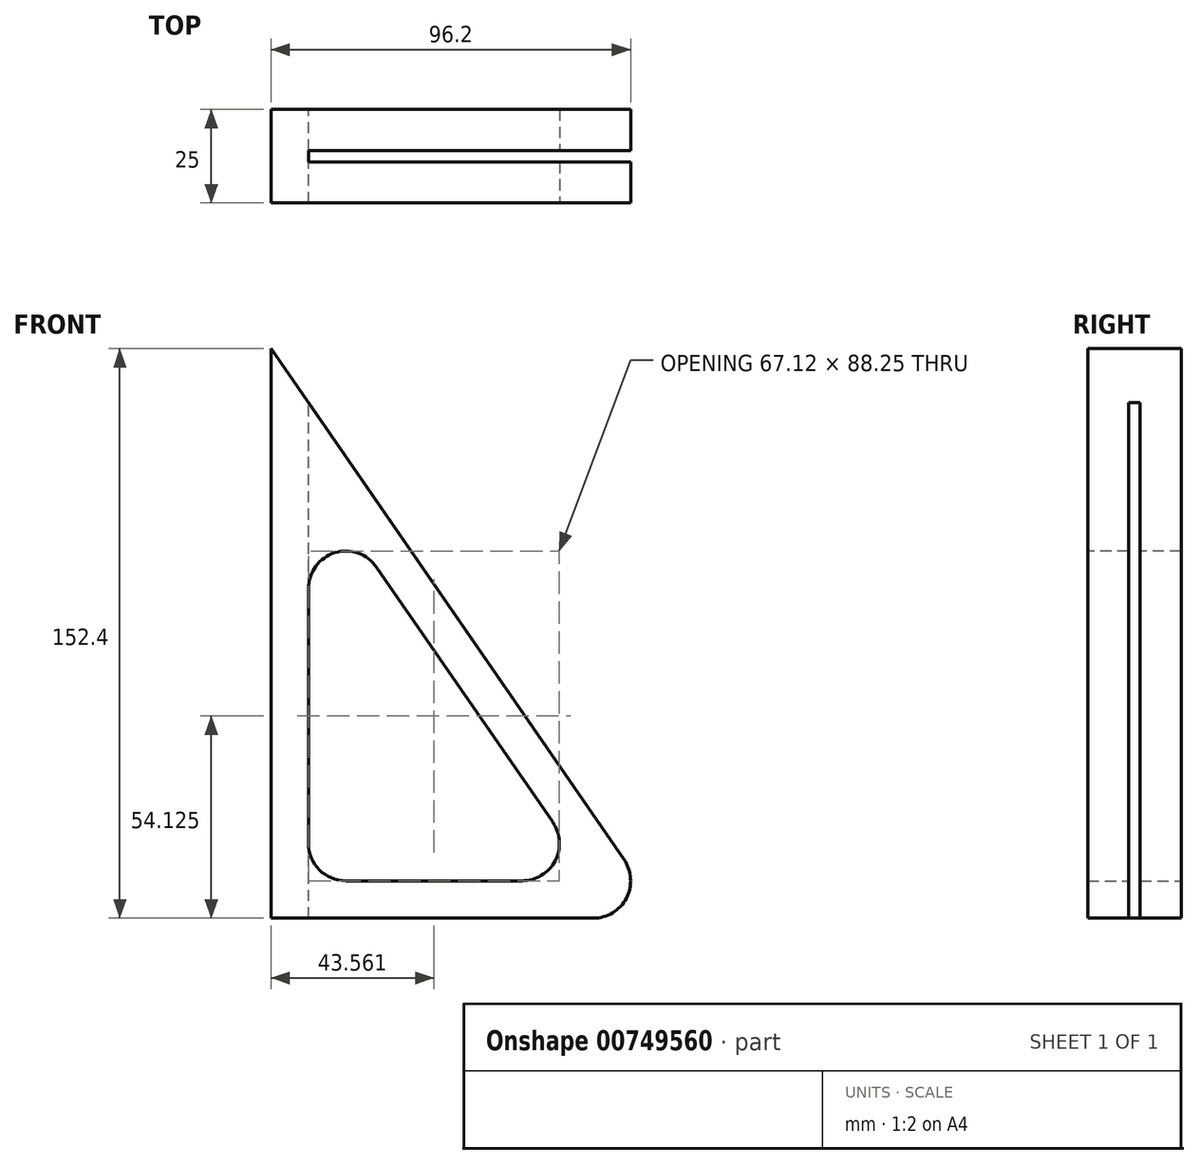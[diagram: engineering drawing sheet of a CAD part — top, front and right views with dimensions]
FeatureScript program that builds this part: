
annotation { "Feature Type Name" : "Feature", "Feature Type Description" : "" }
export const myFeature = defineFeature(function(context is Context, id is Id, definition is map)
    precondition{}
    {
        {
            var Q0;
            Q0=qCreatedBy(makeId("Front.planeOp"),FACE);
            var sketch = newSketch(context, id + "F0", { "sketchPlane" : qUnion([Q0])});
            skLineSegment(sketch, "E0", {"start": v(10, 120.33) * mm, "end": v(10, 10) * mm});
            skLineSegment(sketch, "E1", {"start": v(10, 10) * mm, "end": v(86.2, 10) * mm});
            skLineSegment(sketch, "E2", {"start": v(86.2, 10) * mm, "end": v(10, 120.33) * mm});
            skLineSegment(sketch, "E3", {"start": v(105.26, 10) * mm, "end": v(105.26, 0) * mm});
            skLineSegment(sketch, "E4", {"start": v(105.26, 0) * mm, "end": v(0, 0) * mm});
            skLineSegment(sketch, "E5", {"start": v(0, 0) * mm, "end": v(0, 152.4) * mm});
            skLineSegment(sketch, "E6", {"start": v(0, 152.4) * mm, "end": v(98.35, 10) * mm});
            skLineSegment(sketch, "E7", {"start": v(98.35, 10) * mm, "end": v(105.26, 10) * mm});
            skLineSegment(sketch, "E8", {"start": v(98.35, 10) * mm, "end": v(105.26, 0) * mm});
            skLineSegment(sketch, "E9", {"start": v(86.2, 10) * mm, "end": v(93.1, 0) * mm});
            skSolve(sketch);
        }
        {
            var Q0;
            Q0=makeQuery(id+"F0.imprint","IMPRINT",FACE,{"disambiguationData":[TD([[makeQuery(id+"F0.imprint","IMPRINT",EDGE,{"derivedFrom":sQuery(id+"F0.wireOp",EDGE,"E0")}),-1.0]])]});
            extrude(context, id + "F1", {"entities" : qUnion([Q0]), "depth" : 25 * mm, "offsetDistance" : 25 * mm});
        }
        {
            var Q0;
            Q0=qCreatedBy(makeId("Right.planeOp"),FACE);
            cPlane(context, id + "F2", {"entities" : qUnion([Q0]), "cplaneType" : CPlaneType.OFFSET, "offset" : 163 * mm, "width" : 150 * mm, "height" : 150 * mm});
        }
        {
            var Q0;
            Q0=qCreatedBy(id+"F2.planeOp",FACE);
            var sketch = newSketch(context, id + "F3", { "sketchPlane" : qUnion([Q0])});
            skLineSegment(sketch, "E10.bottom", {"start": v(-10.95, 197.6) * mm, "end": v(-14.05, 197.6) * mm});
            skLineSegment(sketch, "E10.top", {"start": v(-10.95, -197.6) * mm, "end": v(-14.05, -197.6) * mm});
            skLineSegment(sketch, "E10.left", {"start": v(-10.95, 197.6) * mm, "end": v(-10.95, -197.6) * mm});
            skLineSegment(sketch, "E10.right", {"start": v(-14.05, 197.6) * mm, "end": v(-14.05, -197.6) * mm});
            skPoint(sketch, "E10.middle", {"position": v(-12.5, 0) * mm});
            skSolve(sketch);
        }
        {
            var Q0;
            Q0 = qSketchRegion(id + "F3", true);
            var Q1;
            Q1=makeQuery(id+"F1.opExtrude","SWEPT_FACE",FACE,{"disambiguationData":[OSD([sQuery(id+"F0.wireOp",EDGE,"E0")])]});
            extrude(context, id + "F4", {"entities" : qUnion([Q0]), "operationType" : NewBodyOperationType.REMOVE, "endBound" : BoundingType.UP_TO_SURFACE, "oppositeDirection" : true, "depth" : 25 * mm, "endBoundEntityFace" : qUnion([Q1]), "offsetDistance" : 25 * mm});
        }
        {
            var Q0;
            {var subQ0=sQuery(id+"F0.wireOp",EDGE,"E8");var subQ2=sQuery(id+"F0.wireOp",EDGE,"E4");Q0=makeQuery(id+"F4.boolean.opBoolean","SPLIT",EDGE,{"disambiguationData":[TD([makeQuery(id+"F4.opExtrude","SWEPT_FACE",FACE,{"disambiguationData":[OSD([sQuery(id+"F3.wireOp",EDGE,"E10.right")])]})])],"derivedFrom":makeQuery(id+"F1.opExtrude","SWEPT_EDGE",EDGE,{"disambiguationData":[OSD([sQuery(id+"F0.wireOp",EDGE,"E3"),subQ2,subQ0])]})});}
            var Q1;
            {var subQ0=sQuery(id+"F0.wireOp",EDGE,"E8");var subQ2=sQuery(id+"F0.wireOp",EDGE,"E4");Q1=makeQuery(id+"F4.boolean.opBoolean","SPLIT",EDGE,{"disambiguationData":[TD([makeQuery(id+"F4.opExtrude","SWEPT_FACE",FACE,{"disambiguationData":[OSD([sQuery(id+"F3.wireOp",EDGE,"E10.left")])]})])],"derivedFrom":makeQuery(id+"F1.opExtrude","SWEPT_EDGE",EDGE,{"disambiguationData":[OSD([sQuery(id+"F0.wireOp",EDGE,"E3"),subQ2,subQ0])]})});}
            var Q2;
            {var subQ0=sQuery(id+"F3.wireOp",EDGE,"E10.right");var subQ1=sQuery(id+"F0.wireOp",EDGE,"E1");var subQ2=sQuery(id+"F0.wireOp",EDGE,"E0");Q2=makeQuery(id+"F4.boolean.opBoolean","SPLIT",EDGE,{"disambiguationData":[TD([makeQuery(id+"F4.opExtrude","SWEPT_FACE",FACE,{"disambiguationData":[OSD([subQ0])]})])],"derivedFrom":makeQuery(id+"F1.opExtrude","SWEPT_EDGE",EDGE,{"disambiguationData":[OSD([subQ2,subQ1])]})});}
            var Q3;
            {var subQ0=sQuery(id+"F0.wireOp",EDGE,"E1");var subQ1=sQuery(id+"F3.wireOp",EDGE,"E10.left");var subQ2=sQuery(id+"F0.wireOp",EDGE,"E0");Q3=makeQuery(id+"F4.boolean.opBoolean","SPLIT",EDGE,{"disambiguationData":[TD([makeQuery(id+"F4.opExtrude","SWEPT_FACE",FACE,{"disambiguationData":[OSD([subQ1])]})])],"derivedFrom":makeQuery(id+"F1.opExtrude","SWEPT_EDGE",EDGE,{"disambiguationData":[OSD([subQ2,subQ0])]})});}
            var Q4;
            {var subQ0=sQuery(id+"F0.wireOp",EDGE,"E2");var subQ1=sQuery(id+"F3.wireOp",EDGE,"E10.left");var subQ2=sQuery(id+"F0.wireOp",EDGE,"E0");Q4=makeQuery(id+"F4.boolean.opBoolean","SPLIT",EDGE,{"disambiguationData":[TD([makeQuery(id+"F4.opExtrude","SWEPT_FACE",FACE,{"disambiguationData":[OSD([subQ1])]})])],"derivedFrom":makeQuery(id+"F1.opExtrude","SWEPT_EDGE",EDGE,{"disambiguationData":[OSD([subQ2,subQ0])]})});}
            var Q5;
            {var subQ0=sQuery(id+"F3.wireOp",EDGE,"E10.right");var subQ1=sQuery(id+"F0.wireOp",EDGE,"E2");var subQ2=sQuery(id+"F0.wireOp",EDGE,"E0");Q5=makeQuery(id+"F4.boolean.opBoolean","SPLIT",EDGE,{"disambiguationData":[TD([makeQuery(id+"F4.opExtrude","SWEPT_FACE",FACE,{"disambiguationData":[OSD([subQ0])]})])],"derivedFrom":makeQuery(id+"F1.opExtrude","SWEPT_EDGE",EDGE,{"disambiguationData":[OSD([subQ2,subQ1])]})});}
            var Q6;
            {var subQ0=sQuery(id+"F0.wireOp",EDGE,"E2");var subQ1=sQuery(id+"F0.wireOp",EDGE,"E1");Q6=makeQuery(id+"F4.boolean.opBoolean","SPLIT",EDGE,{"disambiguationData":[TD([makeQuery(id+"F4.opExtrude","SWEPT_FACE",FACE,{"disambiguationData":[OSD([sQuery(id+"F3.wireOp",EDGE,"E10.right")])]})])],"derivedFrom":makeQuery(id+"F1.opExtrude","SWEPT_EDGE",EDGE,{"disambiguationData":[OSD([subQ1,subQ0])]})});}
            var Q7;
            {var subQ0=sQuery(id+"F0.wireOp",EDGE,"E2");var subQ1=sQuery(id+"F0.wireOp",EDGE,"E1");Q7=makeQuery(id+"F4.boolean.opBoolean","SPLIT",EDGE,{"disambiguationData":[TD([makeQuery(id+"F4.opExtrude","SWEPT_FACE",FACE,{"disambiguationData":[OSD([sQuery(id+"F3.wireOp",EDGE,"E10.left")])]})])],"derivedFrom":makeQuery(id+"F1.opExtrude","SWEPT_EDGE",EDGE,{"disambiguationData":[OSD([subQ1,subQ0])]})});}
            fillet(context, id + "F5", {"entities" : qUnion([Q0, Q1, Q2, Q3, Q4, Q5, Q6, Q7]), "tangentPropagation" : true, "radius" : 10 * mm, "defaultsChanged" : false, "vertexSettings" : [], "allowEdgeOverflow" : false});
        }
    });
